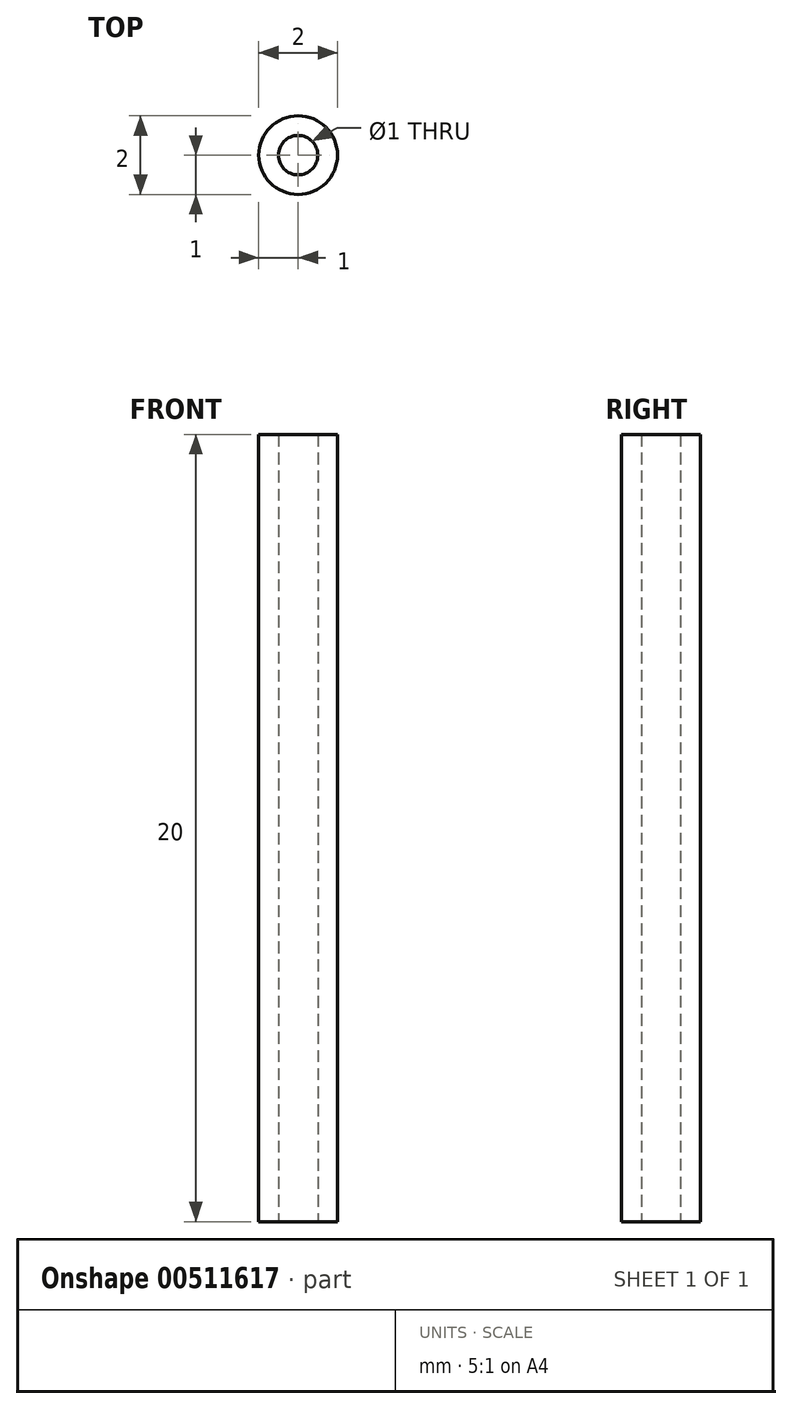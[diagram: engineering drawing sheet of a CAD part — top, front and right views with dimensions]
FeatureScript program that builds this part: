
annotation { "Feature Type Name" : "Feature", "Feature Type Description" : "" }
export const myFeature = defineFeature(function(context is Context, id is Id, definition is map)
    precondition{}
    {
        {
            var Q0;
            Q0=qCreatedBy(makeId("Top.planeOp"),FACE);
            var sketch = newSketch(context, id + "F0", { "sketchPlane" : qUnion([Q0])});
            skCircle(sketch, "E0", {"center": v(0, 0) * mm, "radius": 0.5 * mm});
            skCircle(sketch, "E1", {"center": v(0, 0) * mm, "radius": 1 * mm});
            skSolve(sketch);
        }
        {
            var Q0;
            Q0=makeQuery(id+"F0.imprint","IMPRINT",FACE,{"disambiguationData":[TD([[makeQuery(id+"F0.imprint","IMPRINT",EDGE,{"derivedFrom":sQuery(id+"F0.wireOp",EDGE,"i81wk9N5-qCNI-4WhL-JQ44-KiTBi6n5gR8r")}),1.0]])]});
            var Q1;
            Q1=makeQuery(id+"F0.imprint","IMPRINT",FACE,{"disambiguationData":[TD([[makeQuery(id+"F0.imprint","IMPRINT",EDGE,{"derivedFrom":sQuery(id+"F0.wireOp",EDGE,"P2dCeyrW-3yyO-GLKp-AFtS-Teg8QAAx5zQA")}),1.0]])]});
            var Q2;
            Q2=makeQuery(id+"F0.imprint","IMPRINT",FACE,{"disambiguationData":[TD([[makeQuery(id+"F0.imprint","IMPRINT",EDGE,{"derivedFrom":sQuery(id+"F0.wireOp",EDGE,"eUsNJooS-I5Mt-Ymv3-55p3-Y8ifr9MI58IP")}),1.0]])]});
            var Q3;
            Q3=makeQuery(id+"F0.imprint","IMPRINT",FACE,{"disambiguationData":[TD([[makeQuery(id+"F0.imprint","IMPRINT",EDGE,{"derivedFrom":sQuery(id+"F0.wireOp",EDGE,"E0")}),-1.0]])]});
            extrude(context, id + "F1", {"entities" : qUnion([Q0, Q1, Q2, Q3]), "depth" : 20 * mm});
        }
    });
